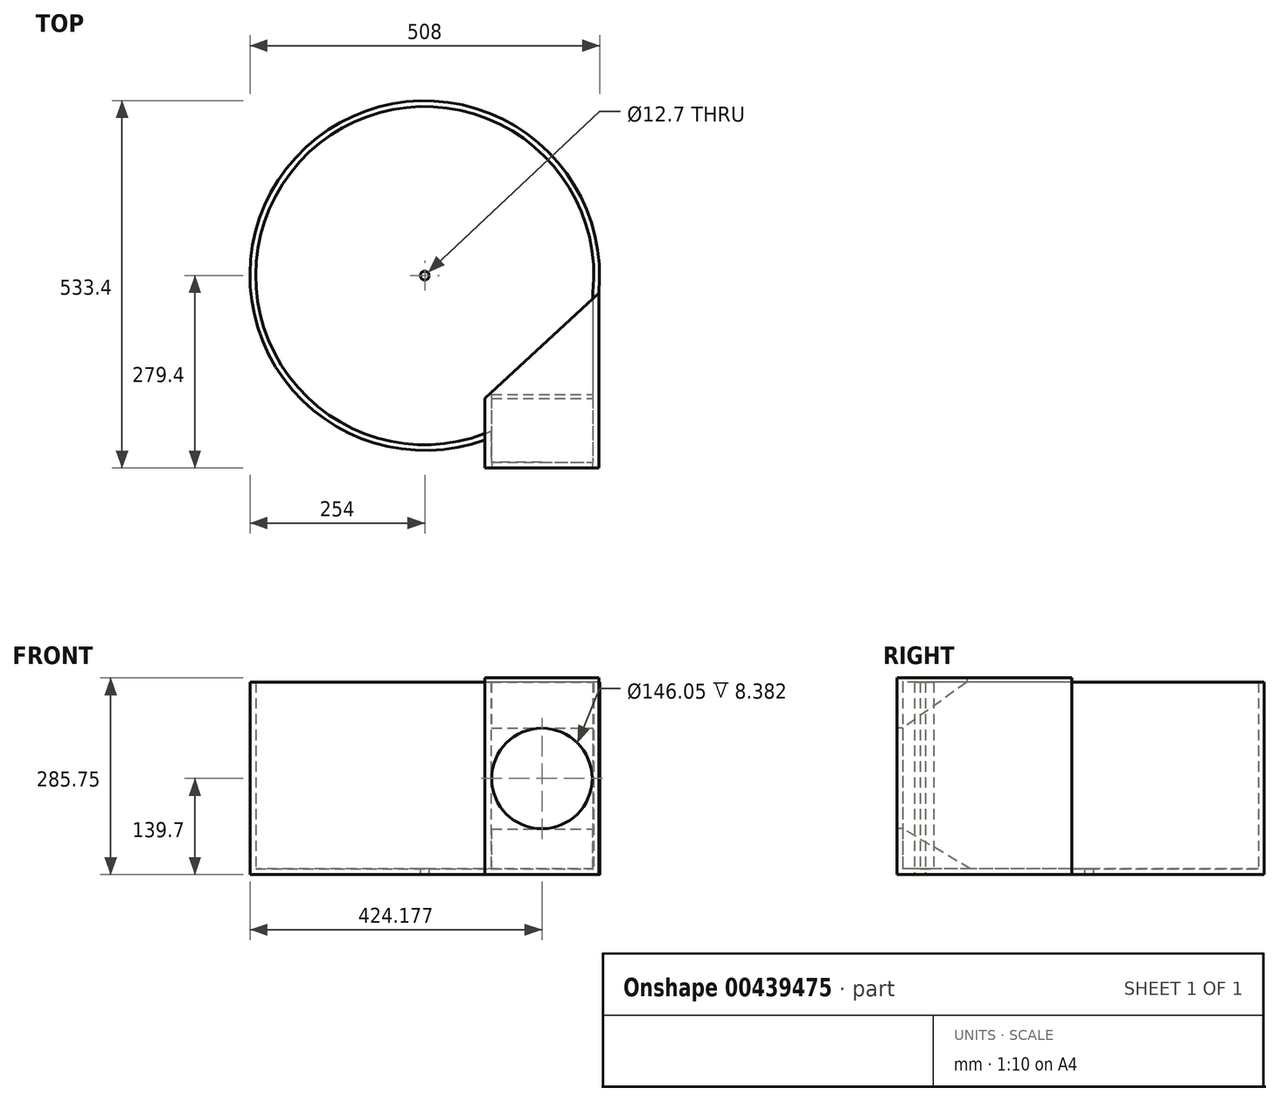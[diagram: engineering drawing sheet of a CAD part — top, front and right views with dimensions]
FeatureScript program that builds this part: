
annotation { "Feature Type Name" : "Feature", "Feature Type Description" : "" }
export const myFeature = defineFeature(function(context is Context, id is Id, definition is map)
    precondition{}
    {
        {
            var Q0;
            Q0=qCreatedBy(makeId("Top.planeOp"),FACE);
            var sketch = newSketch(context, id + "F0", { "sketchPlane" : qUnion([Q0])});
            skCircle(sketch, "E0", {"center": v(0, 0) * mm, "radius": 254 * mm});
            skLineSegment(sketch, "E1.bottom", {"start": v(87.63, -25.4) * mm, "end": v(252.73, -25.4) * mm});
            skLineSegment(sketch, "E1.top", {"start": v(87.63, -279.4) * mm, "end": v(252.73, -279.4) * mm});
            skLineSegment(sketch, "E1.left", {"start": v(87.63, -25.4) * mm, "end": v(87.63, -279.4) * mm});
            skLineSegment(sketch, "E1.right", {"start": v(252.73, -25.4) * mm, "end": v(252.73, -279.4) * mm});
            skSolve(sketch);
        }
        {
            var Q0;
            {var subQ0=sQuery(id+"F0.wireOp",EDGE,"E1.bottom");Q0=makeQuery(id+"F0.imprint","IMPRINT",FACE,{"disambiguationData":[TD([[makeQuery(id+"F0.imprint","IMPRINT",EDGE,{"derivedFrom":subQ0}),1.0]])]});}
            var Q1;
            {var subQ0=sQuery(id+"F0.wireOp",EDGE,"E1.bottom");Q1=makeQuery(id+"F0.imprint","IMPRINT",FACE,{"disambiguationData":[TD([[makeQuery(id+"F0.imprint","IMPRINT",EDGE,{"derivedFrom":subQ0}),-1.0]])]});}
            var Q2;
            {var subQ4=sQuery(id+"F0.wireOp",EDGE,"E1.top");Q2=makeQuery(id+"F0.imprint","IMPRINT",FACE,{"disambiguationData":[TD([[makeQuery(id+"F0.imprint","IMPRINT",EDGE,{"derivedFrom":subQ4}),1.0]])]});}
            extrude(context, id + "F1", {"entities" : qUnion([Q0, Q1, Q2]), "depth" : 279.4 * mm});
        }
        {
            var Q0;
            Q0=makeQuery(id+"F1.opExtrude","SWEPT_FACE",FACE,{"disambiguationData":[OSD([sQuery(id+"F0.wireOp",EDGE,"E1.top")])]});
            var sketch = newSketch(context, id + "F2", { "sketchPlane" : qUnion([Q0])});
            skCircle(sketch, "E2", {"center": v(170.18, 139.7) * mm, "radius": 73.03 * mm});
            skSolve(sketch);
        }
        {
            var Q0;
            Q0=makeQuery(id+"F1.opExtrude","CAP_FACE",FACE,{"disambiguationData":[OSD([sQuery(id+"F0.wireOp",EDGE,"E0"),sQuery(id+"F0.wireOp",EDGE,"E1.top"),sQuery(id+"F0.wireOp",EDGE,"E1.left"),sQuery(id+"F0.wireOp",EDGE,"E1.right")])],"isStart":false});
            shell(context, id + "F3", {"entities" : qUnion([Q0]), "thickness" : 8.38 * mm});
        }
        {
            var Q0;
            Q0=sQuery(id+"F2.wireOp",VERTEX,"E2.center");
            var Q1;
            Q1=makeQuery(id+"F1.opExtrude","SWEPT_BODY",BODY,{"disambiguationData":[OSD([sQuery(id+"F0.wireOp",EDGE,"E0"),sQuery(id+"F0.wireOp",EDGE,"E1.top"),sQuery(id+"F0.wireOp",EDGE,"E1.left"),sQuery(id+"F0.wireOp",EDGE,"E1.right")])]});
            hole(context, id + "F4", {"style" : HoleStyle.SIMPLE, "endStyle" : HoleEndStyle.BLIND, "holeDiameter" : 146.05 * mm, "holeDepth" : 12.7 * mm, "isTappedThrough" : true, "tappedDepth" : 12.7 * mm, "tapClearance" : 3, "locations" : qUnion([Q0]), "scope" : qUnion([Q1])});
        }
        {
            var Q0;
            Q0=makeQuery(id+"F3.opShell","OFFSET_FACE",FACE,{"disambiguationData":[OSD([sQuery(id+"F0.wireOp",EDGE,"E1.right")])]});
            var sketch = newSketch(context, id + "F5", { "sketchPlane" : qUnion([Q0])});
            skLineSegment(sketch, "E3", {"start": v(172.62, 8.38) * mm, "end": v(271.02, 66.55) * mm});
            skLineSegment(sketch, "E4", {"start": v(271.02, 66.55) * mm, "end": v(271.02, 8.38) * mm});
            skLineSegment(sketch, "E5", {"start": v(271.02, 8.38) * mm, "end": v(172.62, 8.38) * mm});
            skLineSegment(sketch, "E6", {"start": v(271.02, 279.4) * mm, "end": v(178.09, 279.4) * mm});
            skLineSegment(sketch, "E7", {"start": v(178.09, 279.4) * mm, "end": v(271.02, 212.85) * mm});
            skLineSegment(sketch, "E8", {"start": v(271.02, 212.85) * mm, "end": v(271.02, 279.4) * mm});
            skSolve(sketch);
        }
        {
            var Q0;
            Q0 = qSketchRegion(id + "F5", true);
            extrude(context, id + "F6", {"entities" : qUnion([Q0]), "operationType" : NewBodyOperationType.ADD, "depth" : 147.32 * mm});
        }
        {
            var Q0;
            Q0=makeQuery(id+"F6.boolean.opBoolean","MERGE",FACE,{"derivedFrom":[makeQuery(id+"F1.opExtrude","CAP_FACE",FACE,{"disambiguationData":[OSD([sQuery(id+"F0.wireOp",EDGE,"E0"),sQuery(id+"F0.wireOp",EDGE,"E1.top"),sQuery(id+"F0.wireOp",EDGE,"E1.left"),sQuery(id+"F0.wireOp",EDGE,"E1.right")])],"isStart":false}),makeQuery(id+"F6.opExtrude","SWEPT_FACE",FACE,{"disambiguationData":[OSD([sQuery(id+"F5.wireOp",EDGE,"E6")])]})]});
            var sketch = newSketch(context, id + "F7", { "sketchPlane" : qUnion([Q0])});
            skLineSegment(sketch, "E9", {"start": v(87.63, -279.4) * mm, "end": v(252.73, -279.4) * mm});
            skLineSegment(sketch, "E10", {"start": v(252.73, -279.4) * mm, "end": v(252.73, -25.4) * mm});
            skLineSegment(sketch, "E11", {"start": v(252.73, -25.4) * mm, "end": v(87.63, -178.09) * mm});
            skLineSegment(sketch, "E12", {"start": v(87.63, -178.09) * mm, "end": v(87.63, -279.4) * mm});
            skSolve(sketch);
        }
        {
            var Q0;
            Q0 = qSketchRegion(id + "F7", true);
            extrude(context, id + "F8", {"entities" : qUnion([Q0]), "operationType" : NewBodyOperationType.ADD, "depth" : 6.35 * mm});
        }
        {
            var Q0;
            Q0=makeQuery(id+"F3.opShell","OFFSET_FACE",FACE,{"disambiguationData":[OSD([sQuery(id+"F0.wireOp",EDGE,"E0"),sQuery(id+"F0.wireOp",EDGE,"E1.top"),sQuery(id+"F0.wireOp",EDGE,"E1.left"),sQuery(id+"F0.wireOp",EDGE,"E1.right")])]});
            var sketch = newSketch(context, id + "F9", { "sketchPlane" : qUnion([Q0])});
            skPoint(sketch, "E13", {"position": v(0, 0) * mm});
            skCircle(sketch, "E14", {"center": v(0, 0) * mm, "radius": 53.11 * mm});
            skSolve(sketch);
        }
        {
            var Q0;
            Q0=sQuery(id+"F9.wireOp",VERTEX,"E13");
            var Q1;
            Q1=makeQuery(id+"F1.opExtrude","SWEPT_BODY",BODY,{"disambiguationData":[OSD([sQuery(id+"F0.wireOp",EDGE,"E0"),sQuery(id+"F0.wireOp",EDGE,"E1.top"),sQuery(id+"F0.wireOp",EDGE,"E1.left"),sQuery(id+"F0.wireOp",EDGE,"E1.right")])]});
            hole(context, id + "F10", {"style" : HoleStyle.SIMPLE, "endStyle" : HoleEndStyle.BLIND, "holeDiameter" : 12.7 * mm, "holeDepth" : 12.7 * mm, "isTappedThrough" : true, "tappedDepth" : 12.7 * mm, "tapClearance" : 3, "locations" : qUnion([Q0]), "scope" : qUnion([Q1])});
        }
    });
